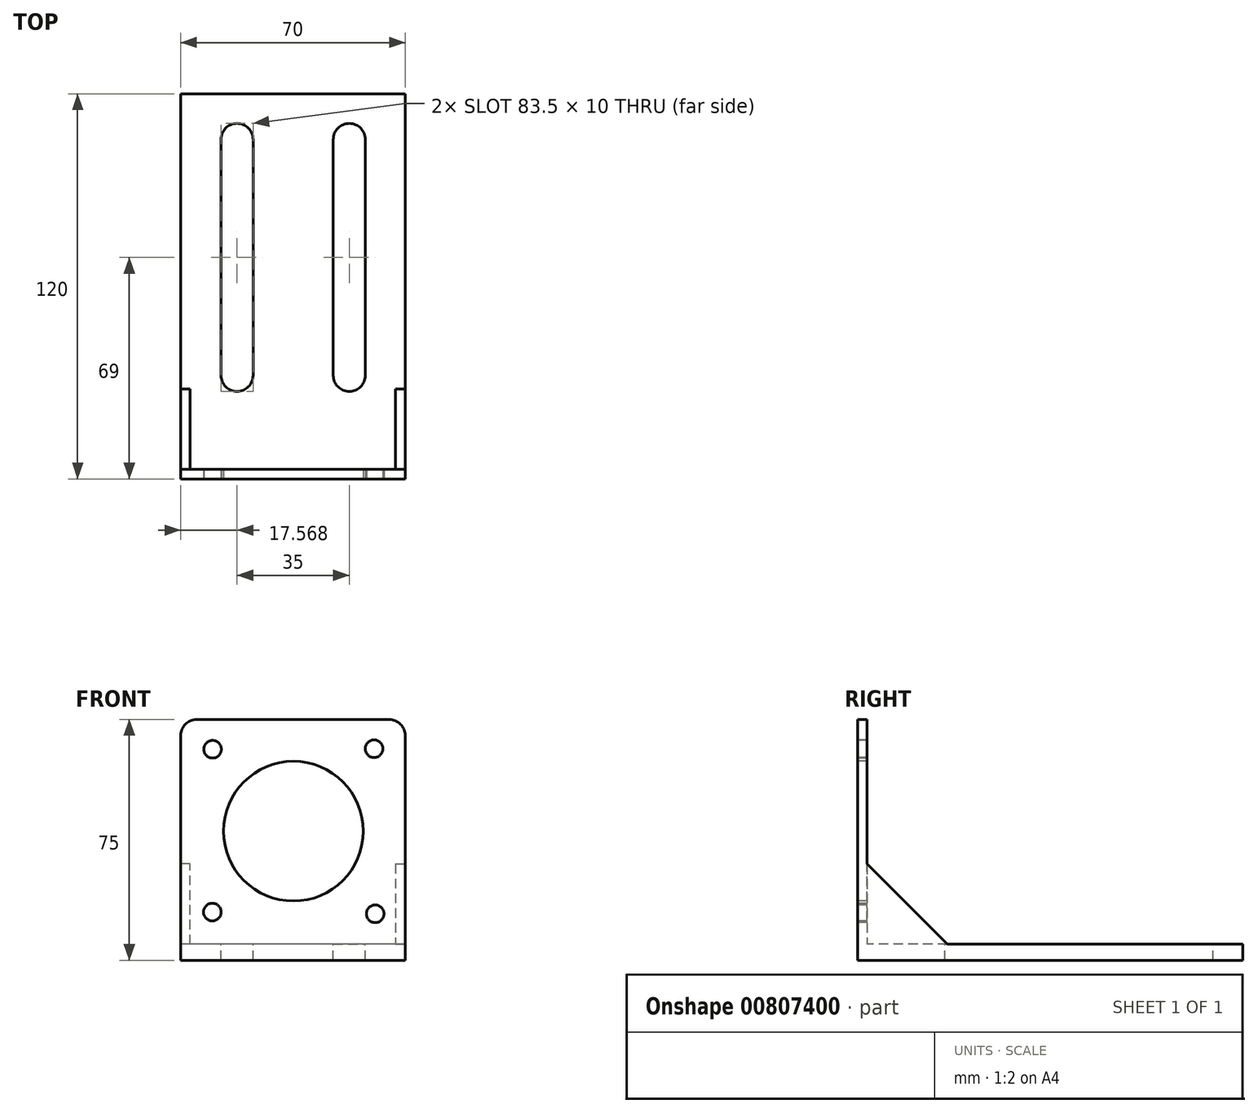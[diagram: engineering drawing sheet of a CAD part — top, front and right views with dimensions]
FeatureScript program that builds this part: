
annotation { "Feature Type Name" : "Feature", "Feature Type Description" : "" }
export const myFeature = defineFeature(function(context is Context, id is Id, definition is map)
    precondition{}
    {
        {
            var Q0;
            Q0=qCreatedBy(makeId("Front.planeOp"),FACE);
            var sketch = newSketch(context, id + "F0", { "sketchPlane" : qUnion([Q0])});
            skLineSegment(sketch, "E0.bottom", {"start": v(29.86, -30.23) * mm, "end": v(-30.14, -30.23) * mm});
            skLineSegment(sketch, "E0.top", {"start": v(29.86, 29.77) * mm, "end": v(-30.14, 29.77) * mm});
            skLineSegment(sketch, "E0.left", {"start": v(29.86, -30.23) * mm, "end": v(29.86, 29.77) * mm});
            skLineSegment(sketch, "E0.right", {"start": v(-30.14, -30.23) * mm, "end": v(-30.14, 29.77) * mm});
            skPoint(sketch, "E0.middle", {"position": v(-0.14, -0.23) * mm});
            skCircle(sketch, "E1", {"center": v(25.14, 25.68) * mm, "radius": 2.75 * mm});
            skCircle(sketch, "E2", {"center": v(-25.19, 25.51) * mm, "radius": 2.75 * mm});
            skCircle(sketch, "E3", {"center": v(-25.26, -25.21) * mm, "radius": 2.75 * mm});
            skCircle(sketch, "E4", {"center": v(25.48, -25.76) * mm, "radius": 2.75 * mm});
            skLineSegment(sketch, "E5", {"start": v(20.67, 29.77) * mm, "end": v(20.67, 22.6) * mm});
            skLineSegment(sketch, "E6", {"start": v(20.67, 22.6) * mm, "end": v(22.7, 20.96) * mm});
            skLineSegment(sketch, "E7", {"start": v(22.7, 20.96) * mm, "end": v(29.86, 20.96) * mm});
            skLineSegment(sketch, "E8", {"start": v(29.86, -20.9) * mm, "end": v(23.58, -20.9) * mm});
            skLineSegment(sketch, "E9", {"start": v(23.58, -20.9) * mm, "end": v(21.05, -23.82) * mm});
            skLineSegment(sketch, "E10", {"start": v(21.05, -23.82) * mm, "end": v(21.05, -30.23) * mm});
            skLineSegment(sketch, "E11", {"start": v(-20.07, -30.23) * mm, "end": v(-20.07, -22.55) * mm});
            skLineSegment(sketch, "E12", {"start": v(-20.07, -22.55) * mm, "end": v(-22.85, -20.02) * mm});
            skLineSegment(sketch, "E13", {"start": v(-22.85, -20.02) * mm, "end": v(-30.14, -20.02) * mm});
            skLineSegment(sketch, "E14", {"start": v(-20.95, 29.77) * mm, "end": v(-20.95, 23.62) * mm});
            skLineSegment(sketch, "E15", {"start": v(-20.95, 23.62) * mm, "end": v(-23.61, 20.96) * mm});
            skLineSegment(sketch, "E16", {"start": v(-23.61, 20.96) * mm, "end": v(-30.14, 20.96) * mm});
            skLineSegment(sketch, "E17", {"start": v(-30.14, -30.23) * mm, "end": v(-35.14, -30.23) * mm});
            skLineSegment(sketch, "E18", {"start": v(-35.14, -30.23) * mm, "end": v(-35.14, 34.77) * mm});
            skLineSegment(sketch, "E19", {"start": v(-35.14, 34.77) * mm, "end": v(34.86, 34.77) * mm});
            skLineSegment(sketch, "E20", {"start": v(34.86, 34.77) * mm, "end": v(34.86, -35.23) * mm});
            skLineSegment(sketch, "E21", {"start": v(34.86, -35.23) * mm, "end": v(-35.14, -35.23) * mm});
            skLineSegment(sketch, "E22", {"start": v(-35.14, -35.23) * mm, "end": v(-35.14, -30.23) * mm});
            skLineSegment(sketch, "E23", {"start": v(-35.14, -35.23) * mm, "end": v(-35.14, -40.23) * mm});
            skLineSegment(sketch, "E24", {"start": v(-35.14, -40.23) * mm, "end": v(34.86, -40.23) * mm});
            skLineSegment(sketch, "E25", {"start": v(34.86, -40.23) * mm, "end": v(34.86, -35.23) * mm});
            skSolve(sketch);
        }
        {
            var Q0;
            Q0=makeQuery(id+"F0.imprint","IMPRINT",FACE,{"disambiguationData":[TD([[makeQuery(id+"F0.imprint","IMPRINT",EDGE,{"derivedFrom":sQuery(id+"F0.wireOp",EDGE,"E18")}),-1.0]])]});
            var Q1;
            {var subQ1=sQuery(id+"F0.wireOp",EDGE,"E5");Q1=makeQuery(id+"F0.imprint","IMPRINT",FACE,{"disambiguationData":[TD([[makeQuery(id+"F0.imprint","IMPRINT",EDGE,{"derivedFrom":subQ1}),-1.0]])]});}
            var Q2;
            Q2=makeQuery(id+"F0.imprint","IMPRINT",FACE,{"disambiguationData":[TD([[makeQuery(id+"F0.imprint","IMPRINT",EDGE,{"derivedFrom":sQuery(id+"F0.wireOp",EDGE,"E2")}),-1.0]])]});
            var Q3;
            Q3=makeQuery(id+"F0.imprint","IMPRINT",FACE,{"disambiguationData":[TD([[makeQuery(id+"F0.imprint","IMPRINT",EDGE,{"derivedFrom":sQuery(id+"F0.wireOp",EDGE,"E1")}),-1.0]])]});
            var Q4;
            Q4=makeQuery(id+"F0.imprint","IMPRINT",FACE,{"disambiguationData":[TD([[makeQuery(id+"F0.imprint","IMPRINT",EDGE,{"derivedFrom":sQuery(id+"F0.wireOp",EDGE,"E3")}),-1.0]])]});
            var Q5;
            Q5=makeQuery(id+"F0.imprint","IMPRINT",FACE,{"disambiguationData":[TD([[makeQuery(id+"F0.imprint","IMPRINT",EDGE,{"derivedFrom":sQuery(id+"F0.wireOp",EDGE,"E4")}),-1.0]])]});
            var Q6;
            Q6 = qSketchRegion(id + "F2", true);
            extrude(context, id + "F1", {"entities" : qUnion([Q0, Q1, Q2, Q3, Q4, Q5, Q6]), "oppositeDirection" : true, "depth" : 3 * mm, "offsetDistance" : 25 * mm});
        }
        {
            var Q0;
            Q0=makeQuery(id+"F1.opExtrude","CAP_FACE",FACE,{"disambiguationData":[OSD([sQuery(id+"F0.wireOp",EDGE,"E1"),sQuery(id+"F0.wireOp",EDGE,"E2"),sQuery(id+"F0.wireOp",EDGE,"E3"),sQuery(id+"F0.wireOp",EDGE,"E4"),sQuery(id+"F0.wireOp",EDGE,"E18"),sQuery(id+"F0.wireOp",EDGE,"E19"),sQuery(id+"F0.wireOp",EDGE,"E20"),sQuery(id+"F0.wireOp",EDGE,"E21"),sQuery(id+"F0.wireOp",EDGE,"E22")])],"isStart":true});
            var sketch = newSketch(context, id + "F2", { "sketchPlane" : qUnion([Q0])});
            skCircle(sketch, "E26", {"center": v(0, 0) * mm, "radius": 21.77 * mm});
            skSolve(sketch);
        }
        {
            var Q0;
            Q0 = qSketchRegion(id + "F2", true);
            extrude(context, id + "F3", {"entities" : qUnion([Q0]), "operationType" : NewBodyOperationType.REMOVE, "oppositeDirection" : true, "depth" : 25 * mm, "offsetDistance" : 25 * mm});
        }
        {
            var Q0;
            Q0=makeQuery(id+"F0.imprint","IMPRINT",FACE,{"disambiguationData":[TD([[makeQuery(id+"F0.imprint","IMPRINT",EDGE,{"derivedFrom":sQuery(id+"F0.wireOp",EDGE,"E21")}),1.0]])]});
            extrude(context, id + "F4", {"entities" : qUnion([Q0]), "operationType" : NewBodyOperationType.ADD, "oppositeDirection" : true, "depth" : 120 * mm, "offsetDistance" : 25 * mm});
        }
        {
            var Q0;
            Q0=makeQuery(id+"F4.opExtrude","SWEPT_FACE",FACE,{"disambiguationData":[OSD([sQuery(id+"F0.wireOp",EDGE,"E21")])]});
            var sketch = newSketch(context, id + "F5", { "sketchPlane" : qUnion([Q0])});
            skLineSegment(sketch, "E27", {"start": v(-35.14, 120) * mm, "end": v(0, 120) * mm});
            skLineSegment(sketch, "E28", {"start": v(0, 120) * mm, "end": v(-17.57, 120) * mm});
            skLineSegment(sketch, "E29", {"start": v(-17.57, 120) * mm, "end": v(-17.57, 3) * mm});
            skLineSegment(sketch, "E30", {"start": v(-17.57, 3) * mm, "end": v(34.86, 3) * mm});
            skLineSegment(sketch, "E31", {"start": v(0, 120) * mm, "end": v(34.86, 120) * mm});
            skLineSegment(sketch, "E32", {"start": v(34.86, 120) * mm, "end": v(17.43, 120) * mm});
            skLineSegment(sketch, "E33", {"start": v(17.43, 120) * mm, "end": v(17.43, 3) * mm});
            skLineSegment(sketch, "E34", {"start": v(-35.14, 120) * mm, "end": v(-35.14, 3) * mm});
            skLineSegment(sketch, "E35", {"start": v(-35.14, 3) * mm, "end": v(-35.14, 61.5) * mm});
            skLineSegment(sketch, "E36", {"start": v(-35.14, 61.5) * mm, "end": v(-35.14, 32.25) * mm});
            skLineSegment(sketch, "E37", {"start": v(-35.14, 32.25) * mm, "end": v(34.86, 32.25) * mm});
            skLineSegment(sketch, "E38", {"start": v(-35.14, 61.5) * mm, "end": v(-35.14, 120) * mm});
            skLineSegment(sketch, "E39", {"start": v(-35.14, 90.75) * mm, "end": v(34.86, 90.75) * mm});
            skCircle(sketch, "E40", {"center": v(-17.57, 90.75) * mm, "radius": 5 * mm});
            skCircle(sketch, "E41", {"center": v(17.43, 90.75) * mm, "radius": 5 * mm});
            skCircle(sketch, "E42", {"center": v(-17.57, 32.25) * mm, "radius": 5 * mm});
            skCircle(sketch, "E43", {"center": v(17.43, 32.25) * mm, "radius": 5 * mm});
            skLineSegment(sketch, "E44", {"start": v(-22.57, 90.75) * mm, "end": v(-22.57, 32.25) * mm});
            skLineSegment(sketch, "E45", {"start": v(-22.57, 32.25) * mm, "end": v(-12.57, 32.25) * mm});
            skLineSegment(sketch, "E46", {"start": v(-12.57, 32.25) * mm, "end": v(-12.57, 90.75) * mm});
            skLineSegment(sketch, "E47", {"start": v(12.43, 90.75) * mm, "end": v(12.43, 32.25) * mm});
            skLineSegment(sketch, "E48", {"start": v(12.43, 32.25) * mm, "end": v(22.43, 32.25) * mm});
            skLineSegment(sketch, "E49", {"start": v(22.43, 32.25) * mm, "end": v(22.43, 90.75) * mm});
            skLineSegment(sketch, "E50", {"start": v(-35.14, 90.75) * mm, "end": v(-35.14, 105.75) * mm});
            skLineSegment(sketch, "E51", {"start": v(-35.14, 105.75) * mm, "end": v(34.86, 105.75) * mm});
            skCircle(sketch, "E52", {"center": v(-17.57, 105.75) * mm, "radius": 5 * mm});
            skCircle(sketch, "E53", {"center": v(17.43, 105.75) * mm, "radius": 5 * mm});
            skLineSegment(sketch, "E54", {"start": v(12.43, 90.75) * mm, "end": v(12.43, 105.75) * mm});
            skLineSegment(sketch, "E55", {"start": v(22.43, 90.75) * mm, "end": v(22.43, 105.75) * mm});
            skLineSegment(sketch, "E56", {"start": v(-12.57, 90.75) * mm, "end": v(-12.57, 105.75) * mm});
            skLineSegment(sketch, "E57", {"start": v(-22.57, 90.75) * mm, "end": v(-22.57, 105.75) * mm});
            skSolve(sketch);
        }
        {
            var Q0;
            {var subQ0=sQuery(id+"F5.wireOp",EDGE,"E40");var subQ1=sQuery(id+"F5.wireOp",EDGE,"E29");var subQ2=makeQuery(id+"F5.imprint","INTERSECT",VERTEX,{"disambiguationData":[OD(0.0)],"derivedFrom":[subQ1,subQ0]});Q0=makeQuery(id+"F5.imprint","IMPRINT",FACE,{"disambiguationData":[TD([[makeQuery(id+"F5.imprint","IMPRINT",EDGE,{"disambiguationData":[TD([[subQ2,-1.0]])],"derivedFrom":subQ1}),1.0]])]});}
            var Q1;
            {var subQ0=sQuery(id+"F5.wireOp",EDGE,"E40");var subQ1=sQuery(id+"F5.wireOp",EDGE,"E29");var subQ2=makeQuery(id+"F5.imprint","INTERSECT",VERTEX,{"disambiguationData":[OD(0.0)],"derivedFrom":[subQ1,subQ0]});Q1=makeQuery(id+"F5.imprint","IMPRINT",FACE,{"disambiguationData":[TD([[makeQuery(id+"F5.imprint","IMPRINT",EDGE,{"disambiguationData":[TD([[subQ2,-1.0]])],"derivedFrom":subQ1}),-1.0]])]});}
            var Q2;
            {var subQ0=sQuery(id+"F5.wireOp",EDGE,"E39");var subQ1=sQuery(id+"F5.wireOp",EDGE,"E29");var subQ2=makeQuery(id+"F5.imprint","INTERSECT",VERTEX,{"derivedFrom":[subQ1,subQ0]});Q2=makeQuery(id+"F5.imprint","IMPRINT",FACE,{"disambiguationData":[TD([[makeQuery(id+"F5.imprint","IMPRINT",EDGE,{"disambiguationData":[TD([[subQ2,-1.0]])],"derivedFrom":subQ1}),-1.0]])]});}
            var Q3;
            {var subQ0=sQuery(id+"F5.wireOp",EDGE,"E39");var subQ1=sQuery(id+"F5.wireOp",EDGE,"E29");var subQ2=makeQuery(id+"F5.imprint","INTERSECT",VERTEX,{"derivedFrom":[subQ1,subQ0]});Q3=makeQuery(id+"F5.imprint","IMPRINT",FACE,{"disambiguationData":[TD([[makeQuery(id+"F5.imprint","IMPRINT",EDGE,{"disambiguationData":[TD([[subQ2,-1.0]])],"derivedFrom":subQ1}),1.0]])]});}
            var Q4;
            {var subQ5=sQuery(id+"F5.wireOp",EDGE,"E46");Q4=makeQuery(id+"F5.imprint","IMPRINT",FACE,{"disambiguationData":[TD([[makeQuery(id+"F5.imprint","IMPRINT",EDGE,{"derivedFrom":subQ5}),1.0]])]});}
            var Q5;
            {var subQ5=sQuery(id+"F5.wireOp",EDGE,"E44");Q5=makeQuery(id+"F5.imprint","IMPRINT",FACE,{"disambiguationData":[TD([[makeQuery(id+"F5.imprint","IMPRINT",EDGE,{"derivedFrom":subQ5}),1.0]])]});}
            var Q6;
            {var subQ0=sQuery(id+"F5.wireOp",EDGE,"E42");var subQ1=sQuery(id+"F5.wireOp",EDGE,"E29");var subQ2=makeQuery(id+"F5.imprint","INTERSECT",VERTEX,{"disambiguationData":[OD(0.0)],"derivedFrom":[subQ1,subQ0]});Q6=makeQuery(id+"F5.imprint","IMPRINT",FACE,{"disambiguationData":[TD([[makeQuery(id+"F5.imprint","IMPRINT",EDGE,{"disambiguationData":[TD([[subQ2,-1.0]])],"derivedFrom":subQ1}),-1.0]])]});}
            var Q7;
            {var subQ0=sQuery(id+"F5.wireOp",EDGE,"E42");var subQ1=sQuery(id+"F5.wireOp",EDGE,"E29");var subQ2=makeQuery(id+"F5.imprint","INTERSECT",VERTEX,{"disambiguationData":[OD(0.0)],"derivedFrom":[subQ1,subQ0]});Q7=makeQuery(id+"F5.imprint","IMPRINT",FACE,{"disambiguationData":[TD([[makeQuery(id+"F5.imprint","IMPRINT",EDGE,{"disambiguationData":[TD([[subQ2,-1.0]])],"derivedFrom":subQ1}),1.0]])]});}
            var Q8;
            {var subQ0=sQuery(id+"F5.wireOp",EDGE,"E45");var subQ1=sQuery(id+"F5.wireOp",EDGE,"E29");var subQ2=makeQuery(id+"F5.imprint","INTERSECT",VERTEX,{"derivedFrom":[subQ1,subQ0]});Q8=makeQuery(id+"F5.imprint","IMPRINT",FACE,{"disambiguationData":[TD([[makeQuery(id+"F5.imprint","IMPRINT",EDGE,{"disambiguationData":[TD([[subQ2,-1.0]])],"derivedFrom":subQ1}),1.0]])]});}
            var Q9;
            {var subQ0=sQuery(id+"F5.wireOp",EDGE,"E45");var subQ1=sQuery(id+"F5.wireOp",EDGE,"E29");var subQ2=makeQuery(id+"F5.imprint","INTERSECT",VERTEX,{"derivedFrom":[subQ1,subQ0]});Q9=makeQuery(id+"F5.imprint","IMPRINT",FACE,{"disambiguationData":[TD([[makeQuery(id+"F5.imprint","IMPRINT",EDGE,{"disambiguationData":[TD([[subQ2,-1.0]])],"derivedFrom":subQ1}),-1.0]])]});}
            var Q10;
            {var subQ5=sQuery(id+"F5.wireOp",EDGE,"E49");Q10=makeQuery(id+"F5.imprint","IMPRINT",FACE,{"disambiguationData":[TD([[makeQuery(id+"F5.imprint","IMPRINT",EDGE,{"derivedFrom":subQ5}),1.0]])]});}
            var Q11;
            {var subQ0=sQuery(id+"F5.wireOp",EDGE,"E39");var subQ1=sQuery(id+"F5.wireOp",EDGE,"E33");var subQ2=makeQuery(id+"F5.imprint","INTERSECT",VERTEX,{"derivedFrom":[subQ1,subQ0]});Q11=makeQuery(id+"F5.imprint","IMPRINT",FACE,{"disambiguationData":[TD([[makeQuery(id+"F5.imprint","IMPRINT",EDGE,{"disambiguationData":[TD([[subQ2,-1.0]])],"derivedFrom":subQ1}),-1.0]])]});}
            var Q12;
            {var subQ0=sQuery(id+"F5.wireOp",EDGE,"E41");var subQ1=sQuery(id+"F5.wireOp",EDGE,"E33");var subQ2=makeQuery(id+"F5.imprint","INTERSECT",VERTEX,{"disambiguationData":[OD(0.0)],"derivedFrom":[subQ1,subQ0]});Q12=makeQuery(id+"F5.imprint","IMPRINT",FACE,{"disambiguationData":[TD([[makeQuery(id+"F5.imprint","IMPRINT",EDGE,{"disambiguationData":[TD([[subQ2,-1.0]])],"derivedFrom":subQ1}),-1.0]])]});}
            var Q13;
            {var subQ0=sQuery(id+"F5.wireOp",EDGE,"E41");var subQ1=sQuery(id+"F5.wireOp",EDGE,"E33");var subQ2=makeQuery(id+"F5.imprint","INTERSECT",VERTEX,{"disambiguationData":[OD(0.0)],"derivedFrom":[subQ1,subQ0]});Q13=makeQuery(id+"F5.imprint","IMPRINT",FACE,{"disambiguationData":[TD([[makeQuery(id+"F5.imprint","IMPRINT",EDGE,{"disambiguationData":[TD([[subQ2,-1.0]])],"derivedFrom":subQ1}),1.0]])]});}
            var Q14;
            {var subQ0=sQuery(id+"F5.wireOp",EDGE,"E39");var subQ1=sQuery(id+"F5.wireOp",EDGE,"E33");var subQ2=makeQuery(id+"F5.imprint","INTERSECT",VERTEX,{"derivedFrom":[subQ1,subQ0]});Q14=makeQuery(id+"F5.imprint","IMPRINT",FACE,{"disambiguationData":[TD([[makeQuery(id+"F5.imprint","IMPRINT",EDGE,{"disambiguationData":[TD([[subQ2,-1.0]])],"derivedFrom":subQ1}),1.0]])]});}
            var Q15;
            {var subQ5=sQuery(id+"F5.wireOp",EDGE,"E47");Q15=makeQuery(id+"F5.imprint","IMPRINT",FACE,{"disambiguationData":[TD([[makeQuery(id+"F5.imprint","IMPRINT",EDGE,{"derivedFrom":subQ5}),1.0]])]});}
            var Q16;
            {var subQ0=sQuery(id+"F5.wireOp",EDGE,"E43");var subQ1=sQuery(id+"F5.wireOp",EDGE,"E33");var subQ2=makeQuery(id+"F5.imprint","INTERSECT",VERTEX,{"disambiguationData":[OD(0.0)],"derivedFrom":[subQ1,subQ0]});Q16=makeQuery(id+"F5.imprint","IMPRINT",FACE,{"disambiguationData":[TD([[makeQuery(id+"F5.imprint","IMPRINT",EDGE,{"disambiguationData":[TD([[subQ2,-1.0]])],"derivedFrom":subQ1}),-1.0]])]});}
            var Q17;
            {var subQ0=sQuery(id+"F5.wireOp",EDGE,"E43");var subQ1=sQuery(id+"F5.wireOp",EDGE,"E33");var subQ2=makeQuery(id+"F5.imprint","INTERSECT",VERTEX,{"disambiguationData":[OD(0.0)],"derivedFrom":[subQ1,subQ0]});Q17=makeQuery(id+"F5.imprint","IMPRINT",FACE,{"disambiguationData":[TD([[makeQuery(id+"F5.imprint","IMPRINT",EDGE,{"disambiguationData":[TD([[subQ2,-1.0]])],"derivedFrom":subQ1}),1.0]])]});}
            var Q18;
            {var subQ0=sQuery(id+"F5.wireOp",EDGE,"E48");var subQ1=sQuery(id+"F5.wireOp",EDGE,"E33");var subQ2=makeQuery(id+"F5.imprint","INTERSECT",VERTEX,{"derivedFrom":[subQ1,subQ0]});Q18=makeQuery(id+"F5.imprint","IMPRINT",FACE,{"disambiguationData":[TD([[makeQuery(id+"F5.imprint","IMPRINT",EDGE,{"disambiguationData":[TD([[subQ2,-1.0]])],"derivedFrom":subQ1}),1.0]])]});}
            var Q19;
            {var subQ0=sQuery(id+"F5.wireOp",EDGE,"E48");var subQ1=sQuery(id+"F5.wireOp",EDGE,"E33");var subQ2=makeQuery(id+"F5.imprint","INTERSECT",VERTEX,{"derivedFrom":[subQ1,subQ0]});Q19=makeQuery(id+"F5.imprint","IMPRINT",FACE,{"disambiguationData":[TD([[makeQuery(id+"F5.imprint","IMPRINT",EDGE,{"disambiguationData":[TD([[subQ2,-1.0]])],"derivedFrom":subQ1}),-1.0]])]});}
            var Q20;
            {var subQ5=sQuery(id+"F5.wireOp",EDGE,"E57");Q20=makeQuery(id+"F5.imprint","IMPRINT",FACE,{"disambiguationData":[TD([[makeQuery(id+"F5.imprint","IMPRINT",EDGE,{"derivedFrom":subQ5}),-1.0]])]});}
            var Q21;
            {var subQ5=sQuery(id+"F5.wireOp",EDGE,"E56");Q21=makeQuery(id+"F5.imprint","IMPRINT",FACE,{"disambiguationData":[TD([[makeQuery(id+"F5.imprint","IMPRINT",EDGE,{"derivedFrom":subQ5}),1.0]])]});}
            var Q22;
            {var subQ5=sQuery(id+"F5.wireOp",EDGE,"E54");Q22=makeQuery(id+"F5.imprint","IMPRINT",FACE,{"disambiguationData":[TD([[makeQuery(id+"F5.imprint","IMPRINT",EDGE,{"derivedFrom":subQ5}),-1.0]])]});}
            var Q23;
            {var subQ5=sQuery(id+"F5.wireOp",EDGE,"E55");Q23=makeQuery(id+"F5.imprint","IMPRINT",FACE,{"disambiguationData":[TD([[makeQuery(id+"F5.imprint","IMPRINT",EDGE,{"derivedFrom":subQ5}),1.0]])]});}
            var Q24;
            {var subQ0=sQuery(id+"F5.wireOp",EDGE,"E51");var subQ1=sQuery(id+"F5.wireOp",EDGE,"E33");var subQ2=makeQuery(id+"F5.imprint","INTERSECT",VERTEX,{"derivedFrom":[subQ1,subQ0]});Q24=makeQuery(id+"F5.imprint","IMPRINT",FACE,{"disambiguationData":[TD([[makeQuery(id+"F5.imprint","IMPRINT",EDGE,{"disambiguationData":[TD([[subQ2,-1.0]])],"derivedFrom":subQ1}),1.0]])]});}
            var Q25;
            {var subQ0=sQuery(id+"F5.wireOp",EDGE,"E53");var subQ1=sQuery(id+"F5.wireOp",EDGE,"E33");var subQ2=makeQuery(id+"F5.imprint","INTERSECT",VERTEX,{"disambiguationData":[OD(0.0)],"derivedFrom":[subQ1,subQ0]});Q25=makeQuery(id+"F5.imprint","IMPRINT",FACE,{"disambiguationData":[TD([[makeQuery(id+"F5.imprint","IMPRINT",EDGE,{"disambiguationData":[TD([[subQ2,-1.0]])],"derivedFrom":subQ1}),1.0]])]});}
            var Q26;
            {var subQ0=sQuery(id+"F5.wireOp",EDGE,"E53");var subQ1=sQuery(id+"F5.wireOp",EDGE,"E33");var subQ2=makeQuery(id+"F5.imprint","INTERSECT",VERTEX,{"disambiguationData":[OD(0.0)],"derivedFrom":[subQ1,subQ0]});Q26=makeQuery(id+"F5.imprint","IMPRINT",FACE,{"disambiguationData":[TD([[makeQuery(id+"F5.imprint","IMPRINT",EDGE,{"disambiguationData":[TD([[subQ2,-1.0]])],"derivedFrom":subQ1}),-1.0]])]});}
            var Q27;
            {var subQ0=sQuery(id+"F5.wireOp",EDGE,"E52");var subQ1=sQuery(id+"F5.wireOp",EDGE,"E29");var subQ2=makeQuery(id+"F5.imprint","INTERSECT",VERTEX,{"disambiguationData":[OD(0.0)],"derivedFrom":[subQ1,subQ0]});Q27=makeQuery(id+"F5.imprint","IMPRINT",FACE,{"disambiguationData":[TD([[makeQuery(id+"F5.imprint","IMPRINT",EDGE,{"disambiguationData":[TD([[subQ2,-1.0]])],"derivedFrom":subQ1}),-1.0]])]});}
            var Q28;
            {var subQ0=sQuery(id+"F5.wireOp",EDGE,"E52");var subQ1=sQuery(id+"F5.wireOp",EDGE,"E29");var subQ2=makeQuery(id+"F5.imprint","INTERSECT",VERTEX,{"disambiguationData":[OD(0.0)],"derivedFrom":[subQ1,subQ0]});Q28=makeQuery(id+"F5.imprint","IMPRINT",FACE,{"disambiguationData":[TD([[makeQuery(id+"F5.imprint","IMPRINT",EDGE,{"disambiguationData":[TD([[subQ2,-1.0]])],"derivedFrom":subQ1}),1.0]])]});}
            var Q29;
            {var subQ0=sQuery(id+"F5.wireOp",EDGE,"E51");var subQ1=sQuery(id+"F5.wireOp",EDGE,"E29");var subQ2=makeQuery(id+"F5.imprint","INTERSECT",VERTEX,{"derivedFrom":[subQ1,subQ0]});Q29=makeQuery(id+"F5.imprint","IMPRINT",FACE,{"disambiguationData":[TD([[makeQuery(id+"F5.imprint","IMPRINT",EDGE,{"disambiguationData":[TD([[subQ2,-1.0]])],"derivedFrom":subQ1}),1.0]])]});}
            var Q30;
            {var subQ0=sQuery(id+"F5.wireOp",EDGE,"E51");var subQ1=sQuery(id+"F5.wireOp",EDGE,"E29");var subQ2=makeQuery(id+"F5.imprint","INTERSECT",VERTEX,{"derivedFrom":[subQ1,subQ0]});Q30=makeQuery(id+"F5.imprint","IMPRINT",FACE,{"disambiguationData":[TD([[makeQuery(id+"F5.imprint","IMPRINT",EDGE,{"disambiguationData":[TD([[subQ2,-1.0]])],"derivedFrom":subQ1}),-1.0]])]});}
            var Q31;
            {var subQ0=sQuery(id+"F5.wireOp",EDGE,"E51");var subQ1=sQuery(id+"F5.wireOp",EDGE,"E33");var subQ2=makeQuery(id+"F5.imprint","INTERSECT",VERTEX,{"derivedFrom":[subQ1,subQ0]});Q31=makeQuery(id+"F5.imprint","IMPRINT",FACE,{"disambiguationData":[TD([[makeQuery(id+"F5.imprint","IMPRINT",EDGE,{"disambiguationData":[TD([[subQ2,-1.0]])],"derivedFrom":subQ1}),-1.0]])]});}
            extrude(context, id + "F6", {"entities" : qUnion([Q0, Q1, Q2, Q3, Q4, Q5, Q6, Q7, Q8, Q9, Q10, Q11, Q12, Q13, Q14, Q15, Q16, Q17, Q18, Q19, Q20, Q21, Q22, Q23, Q24, Q25, Q26, Q27, Q28, Q29, Q30, Q31]), "operationType" : NewBodyOperationType.REMOVE, "oppositeDirection" : true, "depth" : 25 * mm, "offsetDistance" : 25 * mm});
        }
        {
            var Q0;
            Q0=makeQuery(id+"F1.opExtrude","SWEPT_EDGE",EDGE,{"disambiguationData":[OSD([sQuery(id+"F0.wireOp",EDGE,"E18"),sQuery(id+"F0.wireOp",EDGE,"E19")])]});
            var Q1;
            Q1=makeQuery(id+"F1.opExtrude","SWEPT_EDGE",EDGE,{"disambiguationData":[OSD([sQuery(id+"F0.wireOp",EDGE,"E19"),sQuery(id+"F0.wireOp",EDGE,"E20")])]});
            fillet(context, id + "F7", {"entities" : qUnion([Q0, Q1]), "radius" : 5 * mm, "tangentPropagation" : true, "allowEdgeOverflow" : false});
        }
        {
            var Q0;
            Q0=makeQuery(id+"F4.boolean.opBoolean","MERGE",FACE,{"derivedFrom":[makeQuery(id+"F1.opExtrude","SWEPT_FACE",FACE,{"disambiguationData":[OSD([sQuery(id+"F0.wireOp",EDGE,"E18"),sQuery(id+"F0.wireOp",EDGE,"E22")])]}),makeQuery(id+"F4.opExtrude","SWEPT_FACE",FACE,{"disambiguationData":[OSD([sQuery(id+"F0.wireOp",EDGE,"E23")])]})]});
            var sketch = newSketch(context, id + "F8", { "sketchPlane" : qUnion([Q0])});
            skLineSegment(sketch, "E58", {"start": v(-3, -35.23) * mm, "end": v(-28, -35.23) * mm});
            skLineSegment(sketch, "E59", {"start": v(-28, -35.23) * mm, "end": v(-3, -35.23) * mm});
            skLineSegment(sketch, "E60", {"start": v(-3, -35.23) * mm, "end": v(-3, -10.23) * mm});
            skLineSegment(sketch, "E61", {"start": v(-3, -10.23) * mm, "end": v(-28, -35.23) * mm});
            skSolve(sketch);
        }
        {
            var Q0;
            Q0 = qSketchRegion(id + "F8", true);
            extrude(context, id + "F9", {"entities" : qUnion([Q0]), "operationType" : NewBodyOperationType.ADD, "oppositeDirection" : true, "depth" : 3 * mm, "offsetDistance" : 25 * mm});
        }
        {
            var Q0;
            Q0=makeQuery(id+"F4.boolean.opBoolean","MERGE",FACE,{"derivedFrom":[makeQuery(id+"F1.opExtrude","SWEPT_FACE",FACE,{"disambiguationData":[OSD([sQuery(id+"F0.wireOp",EDGE,"E20")])]}),makeQuery(id+"F4.opExtrude","SWEPT_FACE",FACE,{"disambiguationData":[OSD([sQuery(id+"F0.wireOp",EDGE,"E25")])]})]});
            var sketch = newSketch(context, id + "F10", { "sketchPlane" : qUnion([Q0])});
            skLineSegment(sketch, "E62", {"start": v(3, -35.23) * mm, "end": v(3, -10.23) * mm});
            skLineSegment(sketch, "E63", {"start": v(3, -35.23) * mm, "end": v(28, -35.23) * mm});
            skLineSegment(sketch, "E64", {"start": v(28, -35.23) * mm, "end": v(3, -10.23) * mm});
            skSolve(sketch);
        }
        {
            var Q0;
            Q0 = qSketchRegion(id + "F10", true);
            extrude(context, id + "F11", {"entities" : qUnion([Q0]), "operationType" : NewBodyOperationType.ADD, "oppositeDirection" : true, "depth" : 3 * mm, "offsetDistance" : 25 * mm});
        }
    });
